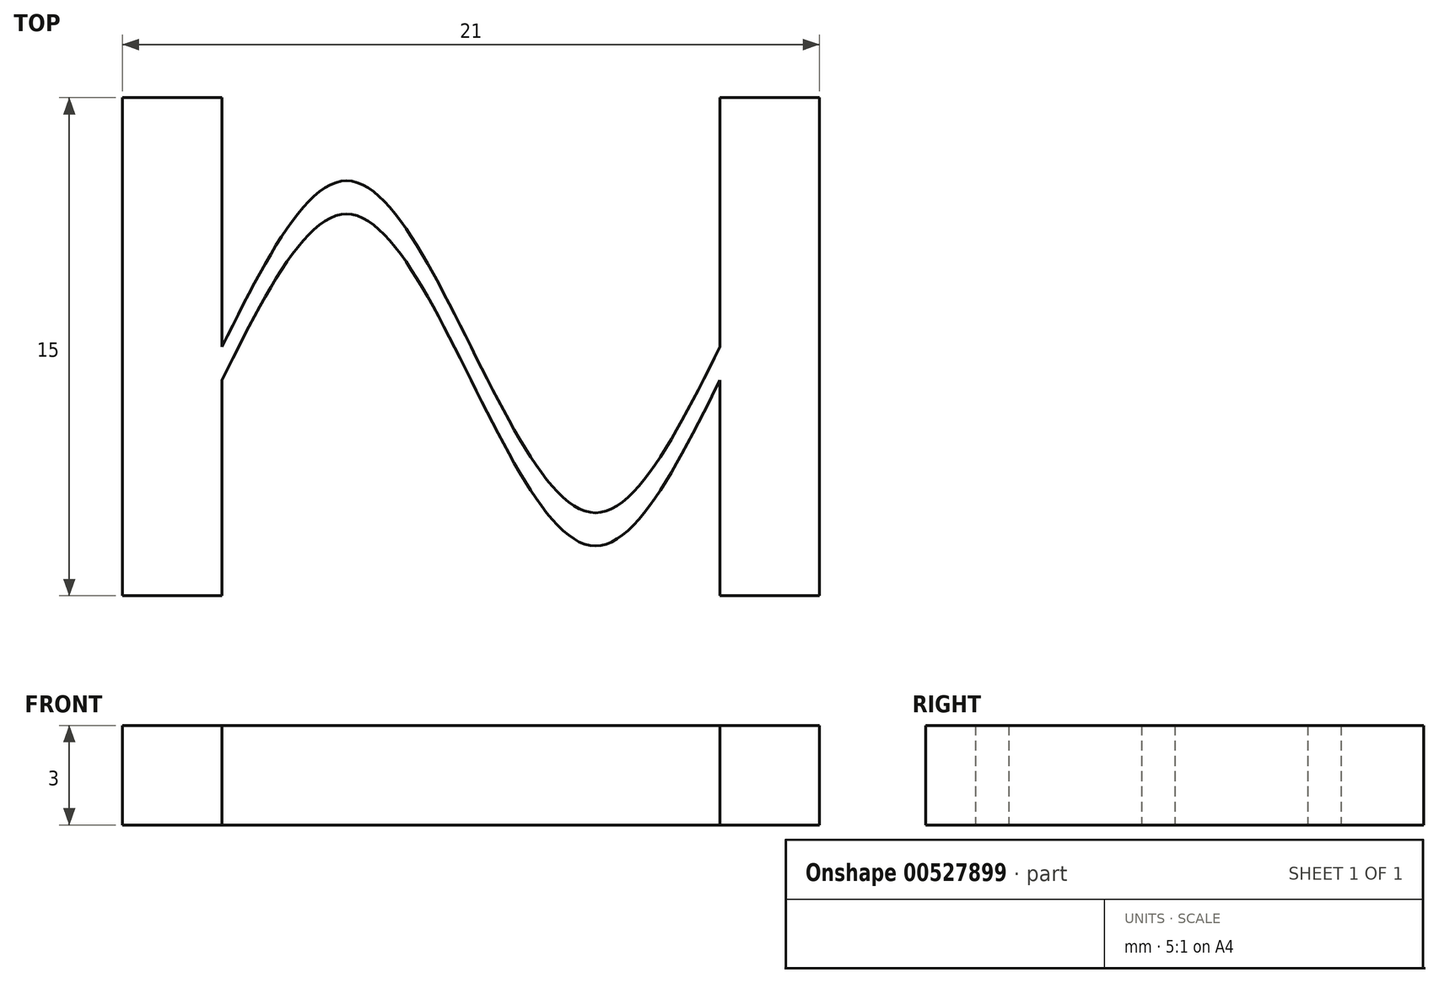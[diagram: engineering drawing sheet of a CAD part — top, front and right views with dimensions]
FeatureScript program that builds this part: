
annotation { "Feature Type Name" : "Feature", "Feature Type Description" : "" }
export const myFeature = defineFeature(function(context is Context, id is Id, definition is map)
    precondition{}
    {
        {
            var Q0;
            Q0=qCreatedBy(makeId("Top.planeOp"),FACE);
            var sketch = newSketch(context, id + "F0", { "sketchPlane" : qUnion([Q0])});
            skLineSegment(sketch, "E0", {"start": v(0, 0) * mm, "end": v(0, 15) * mm});
            skLineSegment(sketch, "E1", {"start": v(0, 15) * mm, "end": v(3, 15) * mm});
            skLineSegment(sketch, "E2", {"start": v(0, 0) * mm, "end": v(3, 0) * mm});
            skLineSegment(sketch, "E3", {"start": v(3, 7.5) * mm, "end": v(18, 7.5) * mm, "construction": true});
            skLineSegment(sketch, "E4", {"start": v(3, 7.5) * mm, "end": v(10.5, 7.5) * mm, "construction": true});
            skLineSegment(sketch, "E5", {"start": v(10.5, 7.5) * mm, "end": v(18, 7.5) * mm, "construction": true});
            skLineSegment(sketch, "E6", {"start": v(6.75, 7.5) * mm, "end": v(6.75, 12.5) * mm, "construction": true});
            skLineSegment(sketch, "E7", {"start": v(14.25, 7.5) * mm, "end": v(14.25, 2.5) * mm, "construction": true});
            skLineSegment(sketch, "E8", {"start": v(18, 0) * mm, "end": v(21, 0) * mm});
            skLineSegment(sketch, "E9", {"start": v(21, 0) * mm, "end": v(21, 15) * mm});
            skLineSegment(sketch, "E10", {"start": v(21, 15) * mm, "end": v(18, 15) * mm});
            skFitSpline(sketch, "E11", {"points": [v(3, 7.5) * mm, v(6.75, 12.5) * mm, v(10.5, 7.5) * mm, v(14.25, 2.5) * mm, v(18, 7.5) * mm], "startDerivative": vector(15, 30) * mm, "endDerivative": vector(15, 30) * mm});
            skLineSegment(sketch, "E12", {"start": v(3, 7.5) * mm, "end": v(3, 6.5) * mm});
            skLineSegment(sketch, "E13", {"start": v(6.75, 12.5) * mm, "end": v(6.75, 11.5) * mm});
            skLineSegment(sketch, "E14", {"start": v(10.5, 7.5) * mm, "end": v(10.5, 6.5) * mm});
            skLineSegment(sketch, "E15", {"start": v(14.25, 2.5) * mm, "end": v(14.25, 1.5) * mm});
            skLineSegment(sketch, "E16", {"start": v(18, 7.5) * mm, "end": v(18, 6.5) * mm});
            skFitSpline(sketch, "E17", {"points": [v(3, 6.5) * mm, v(6.75, 11.5) * mm, v(10.5, 6.5) * mm, v(14.25, 1.5) * mm, v(18, 6.5) * mm], "startDerivative": vector(15, 30) * mm, "endDerivative": vector(15, 30) * mm});
            skLineSegment(sketch, "E18", {"start": v(18, 15) * mm, "end": v(18, 7.5) * mm});
            skLineSegment(sketch, "E19", {"start": v(3, 15) * mm, "end": v(3, 7.5) * mm});
            skLineSegment(sketch, "E20", {"start": v(3, 6.5) * mm, "end": v(3, 0) * mm});
            skLineSegment(sketch, "E21", {"start": v(18, 6.5) * mm, "end": v(18, 0) * mm});
            skSolve(sketch);
        }
        {
            var Q0;
            Q0=qSketchRegion(id+"F0",true);
            extrude(context, id + "F1", {"entities" : qUnion([Q0]), "depth" : 3 * mm});
        }
    });
